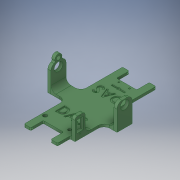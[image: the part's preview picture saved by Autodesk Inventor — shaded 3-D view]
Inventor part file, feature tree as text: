
AUTODESK INVENTOR PART (.ipt)
format: ipt  version: 2017 (Build 210142000, 142)  size: 606,720 bytes
history: mixed  units: in
note: dims shown in document units (in); Inventor stores cm internally (conversion verified against a paired STEP export)
features: fillet x5, other x5, extrude x2, sketch x2, projected_geometry x2, imported_body x1
ambient origin geometry x8: Origin, YZ Plane, XZ Plane, XY Plane, X Axis, Y Axis, Z Axis, Center Point
bodies: Solid1 (imported_parasolid), Solid2 (imported_parasolid), Solid3 (imported_parasolid), Solid4 (imported_parasolid), Solid5 (imported_parasolid)
feature tree (17):
  extrude  "Extrusion1"  Depth=0.4306in TaperAngle=0.0deg
  extrude  "Extrusion2"  Depth=0.4537in
  fillet  "Fillet2"  Radius=0.4537in
  fillet  "Fillet3"  Radius=0.4537in
  fillet  "Fillet4"  Radius=0.4537in
  fillet  "Fillet5"  [1 undecoded]
  fillet  "Fillet6"  [1 undecoded]
  sketch  "Sketch1"  dims[d0=0.1181in d1=0.0in d3=0.4306in d4=0.0in]
  projected_geometry  "Projected Loop1"
  sketch  "Sketch2"  dims[d5=0.4537in d6=0.4537in d7=0.4537in d8=0.4537in d9=0.4537in]
  projected_geometry  "Projected Loop2"
  other  "Corte-extrusão5[1]"
  other  "Corte-extrusão5[2]"
  other  "Corte-extrusão5[3]"
  other  "Corte-extrusão5[4]"
  other  "Corte-extrusão5[5]"
  imported_body  NMx_Import_Brep_tag  [imported B-rep: ~22 faces, bbox_mm=None]
note: 2 required parameter values undecoded (feature->parameter linkage not recoverable at this tier; creation-order binding heuristic only, values carry confidence <= 0.55)
